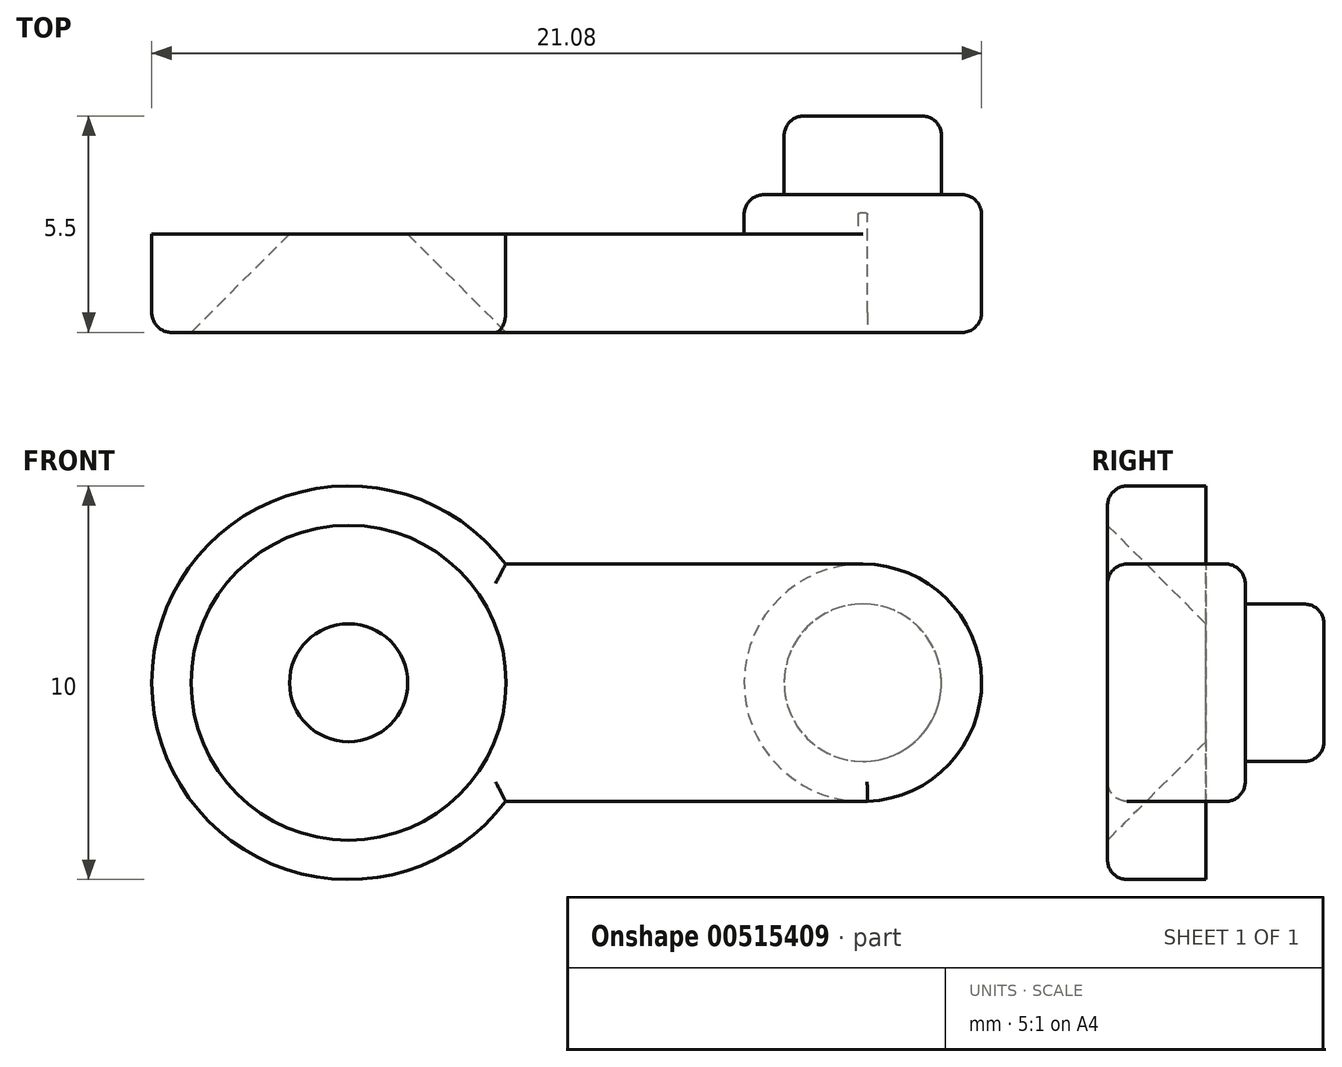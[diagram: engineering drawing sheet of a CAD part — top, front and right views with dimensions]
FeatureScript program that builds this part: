
annotation { "Feature Type Name" : "Feature", "Feature Type Description" : "" }
export const myFeature = defineFeature(function(context is Context, id is Id, definition is map)
    precondition{}
    {
        {
            var Q0;
            Q0=qCreatedBy(makeId("Front.planeOp"),FACE);
            var sketch = newSketch(context, id + "F0", { "sketchPlane" : qUnion([Q0])});
            skCircle(sketch, "E0", {"center": v(0, 0) * mm, "radius": 1.5 * mm});
            skLineSegment(sketch, "E1.top", {"start": v(0.06, 3.02) * mm, "end": v(13.06, 3.02) * mm});
            skArc(sketch, "E2", {"start": v(13.06, 3.02) * mm, "mid": v(16.08, 0.06) * mm, "end": v(13.18, -3.01) * mm});
            skLineSegment(sketch, "E3", {"start": v(19.5, 0) * mm, "end": v(-7.8, 0) * mm});
            skLineSegment(sketch, "E4", {"start": v(13.18, -3.01) * mm, "end": v(0, -3.01) * mm});
            skArc(sketch, "E5", {"start": v(3.99, -3.01) * mm, "mid": v(-5, 0) * mm, "end": v(3.99, 3.02) * mm});
            skSolve(sketch);
        }
        {
            var Q0;
            {var subQ1=sQuery(id+"F0.wireOp",EDGE,"E3");var subQ3=sQuery(id+"F0.wireOp",EDGE,"E0");var subQ7=makeQuery(id+"F0.imprint","INTERSECT",VERTEX,{"disambiguationData":[OD(0.0)],"derivedFrom":[subQ3,subQ1]});Q0=makeQuery(id+"F0.imprint","IMPRINT",FACE,{"disambiguationData":[TD([[makeQuery(id+"F0.imprint","IMPRINT",EDGE,{"disambiguationData":[TD([[subQ7,1.0]])],"derivedFrom":subQ3}),-1.0]])]});}
            var Q1;
            {var subQ3=sQuery(id+"F0.wireOp",EDGE,"E3");var subQ7=sQuery(id+"F0.wireOp",EDGE,"E0");var subQ8=makeQuery(id+"F0.imprint","INTERSECT",VERTEX,{"disambiguationData":[OD(0.0)],"derivedFrom":[subQ7,subQ3]});Q1=makeQuery(id+"F0.imprint","IMPRINT",FACE,{"disambiguationData":[TD([[makeQuery(id+"F0.imprint","IMPRINT",EDGE,{"disambiguationData":[TD([[subQ8,-1.0]])],"derivedFrom":subQ7}),-1.0]])]});}
            extrude(context, id + "F1", {"entities" : qUnion([Q0, Q1]), "depth" : 2.5 * mm, "offsetDistance" : 25 * mm});
        }
        {
            var Q0;
            Q0=makeQuery(id+"F1.opExtrude","CAP_FACE",FACE,{"disambiguationData":[OSD([sQuery(id+"F0.wireOp",EDGE,"E0"),sQuery(id+"F0.wireOp",EDGE,"E1.top"),sQuery(id+"F0.wireOp",EDGE,"E2"),sQuery(id+"F0.wireOp",EDGE,"E4"),sQuery(id+"F0.wireOp",EDGE,"E5")])],"isStart":true});
            var sketch = newSketch(context, id + "F2", { "sketchPlane" : qUnion([Q0])});
            skCircle(sketch, "E6", {"center": v(-13.06, 0) * mm, "radius": 3.02 * mm});
            skCircle(sketch, "E7", {"center": v(-13.06, 0) * mm, "radius": 2 * mm});
            skSolve(sketch);
        }
        {
            var Q0;
            Q0=makeQuery(id+"F2.imprint","IMPRINT",FACE,{"disambiguationData":[TD([[makeQuery(id+"F2.imprint","IMPRINT",EDGE,{"derivedFrom":sQuery(id+"F2.wireOp",EDGE,"E7")}),-1.0]])]});
            extrude(context, id + "F3", {"entities" : qUnion([Q0]), "operationType" : NewBodyOperationType.ADD, "depth" : 1 * mm, "offsetDistance" : 25 * mm});
        }
        {
            var Q0;
            Q0=makeQuery(id+"F3.boolean.opBoolean","SPLIT",FACE,{"disambiguationData":[TD([makeQuery(id+"F3.opExtrude","SWEPT_FACE",FACE,{"disambiguationData":[OSD([sQuery(id+"F2.wireOp",EDGE,"E7")])]})])],"derivedFrom":makeQuery(id+"F1.opExtrude","CAP_FACE",FACE,{"disambiguationData":[OSD([sQuery(id+"F0.wireOp",EDGE,"E0"),sQuery(id+"F0.wireOp",EDGE,"E1.top"),sQuery(id+"F0.wireOp",EDGE,"E2"),sQuery(id+"F0.wireOp",EDGE,"E4"),sQuery(id+"F0.wireOp",EDGE,"E5")])],"isStart":true})});
            extrude(context, id + "F4", {"entities" : qUnion([Q0]), "operationType" : NewBodyOperationType.ADD, "depth" : 3 * mm, "offsetDistance" : 25 * mm});
        }
        {
            var Q0;
            Q0=makeQuery(id+"F4.opExtrude","CAP_EDGE",EDGE,{"disambiguationData":[OSD([sQuery(id+"F2.wireOp",EDGE,"E7")])],"isStart":false});
            var Q1;
            Q1=makeQuery(id+"F3.opExtrude","CAP_EDGE",EDGE,{"disambiguationData":[OSD([sQuery(id+"F2.wireOp",EDGE,"E6")])],"isStart":false});
            var Q2;
            Q2=makeQuery(id+"F1.opExtrude","CAP_EDGE",EDGE,{"disambiguationData":[OSD([sQuery(id+"F0.wireOp",EDGE,"E5")])],"isStart":false});
            fillet(context, id + "F5", {"entities" : qUnion([Q0, Q1, Q2]), "radius" : .5 * mm, "tangentPropagation" : true, "allowEdgeOverflow" : false});
        }
        {
            var Q0;
            Q0=makeQuery(id+"F1.opExtrude","CAP_EDGE",EDGE,{"disambiguationData":[OSD([sQuery(id+"F0.wireOp",EDGE,"E1.top")])],"isStart":false});
            var Q1;
            Q1=makeQuery(id+"F1.opExtrude","CAP_EDGE",EDGE,{"disambiguationData":[OSD([sQuery(id+"F0.wireOp",EDGE,"E2")])],"isStart":false});
            var Q2;
            Q2=makeQuery(id+"F1.opExtrude","CAP_EDGE",EDGE,{"disambiguationData":[OSD([sQuery(id+"F0.wireOp",EDGE,"E4")])],"isStart":false});
            fillet(context, id + "F6", {"entities" : qUnion([Q0, Q1, Q2]), "radius" : .5 * mm, "tangentPropagation" : true, "allowEdgeOverflow" : false});
        }
        {
            var Q0;
            Q0=makeQuery(id+"F1.opExtrude","CAP_EDGE",EDGE,{"disambiguationData":[OSD([sQuery(id+"F0.wireOp",EDGE,"E0")])],"isStart":false});
            chamfer(context, id + "F7", {"entities" : qUnion([Q0]), "width" : 2.5 * mm, "tangentPropagation" : true});
        }
    });
